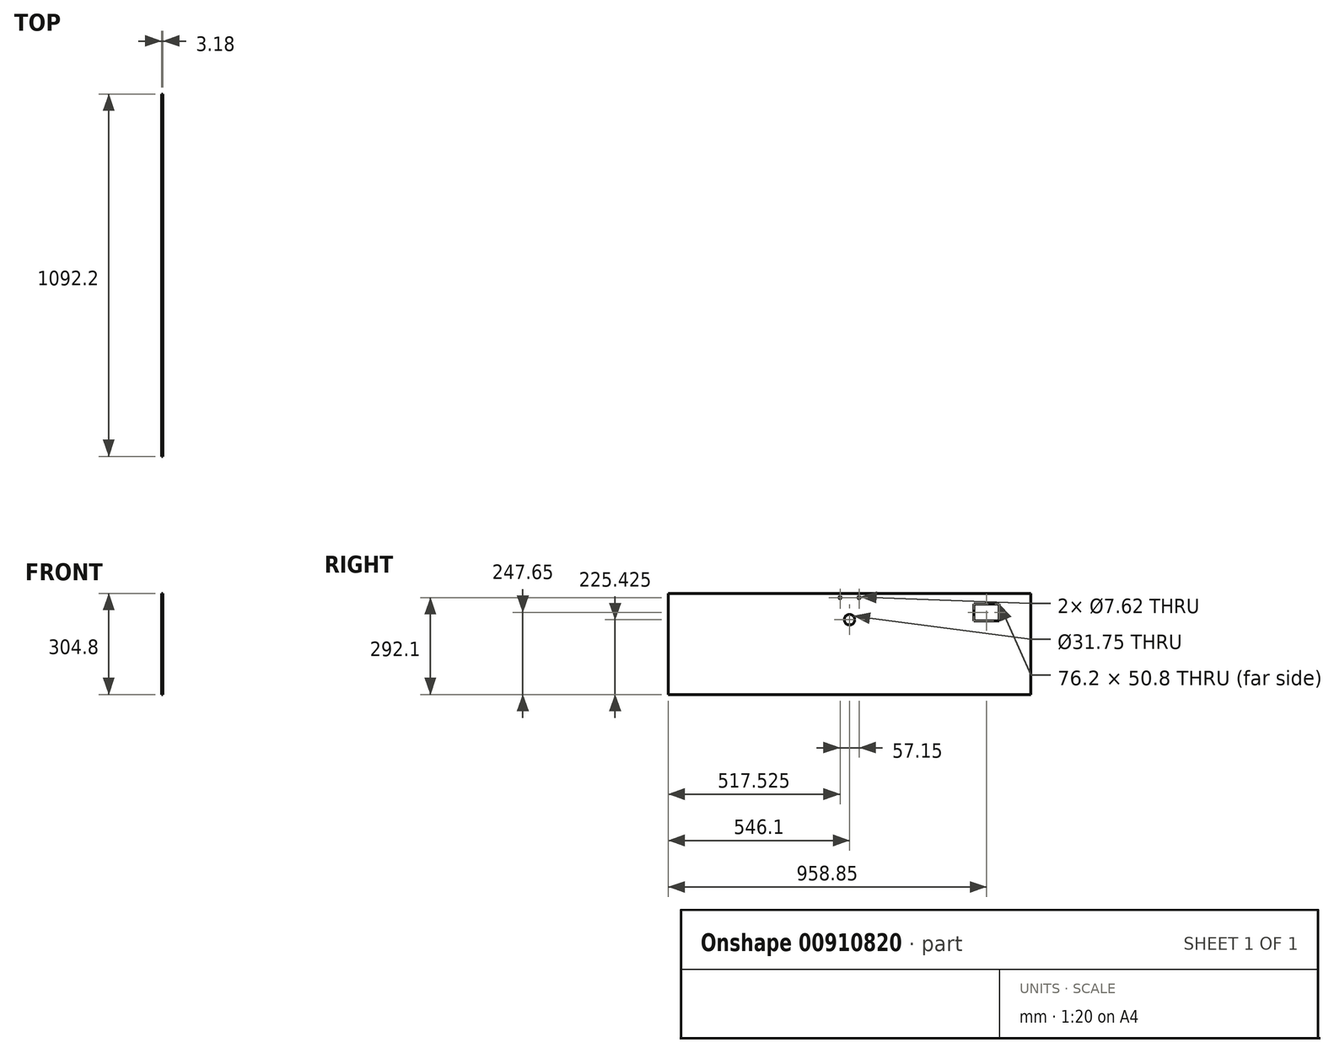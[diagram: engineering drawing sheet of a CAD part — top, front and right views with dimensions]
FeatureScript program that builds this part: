
annotation { "Feature Type Name" : "Feature", "Feature Type Description" : "" }
export const myFeature = defineFeature(function(context is Context, id is Id, definition is map)
    precondition{}
    {
        {
            var Q0;
            Q0=qCreatedBy(makeId("Right.planeOp"),FACE);
            var sketch = newSketch(context, id + "F0", { "sketchPlane" : qUnion([Q0])});
            skLineSegment(sketch, "E0.bottom", {"start": v(0, 0) * mm, "end": v(1092.2, 0) * mm});
            skLineSegment(sketch, "E0.top", {"start": v(0, 304.8) * mm, "end": v(1092.2, 304.8) * mm});
            skLineSegment(sketch, "E0.left", {"start": v(0, 0) * mm, "end": v(0, 304.8) * mm});
            skLineSegment(sketch, "E0.right", {"start": v(1092.2, 0) * mm, "end": v(1092.2, 304.8) * mm});
            skLineSegment(sketch, "E1.bottom", {"start": v(920.75, 222.25) * mm, "end": v(996.95, 222.25) * mm});
            skLineSegment(sketch, "E1.top", {"start": v(920.75, 273.05) * mm, "end": v(996.95, 273.05) * mm});
            skLineSegment(sketch, "E1.left", {"start": v(920.75, 222.25) * mm, "end": v(920.75, 273.05) * mm});
            skLineSegment(sketch, "E1.right", {"start": v(996.95, 222.25) * mm, "end": v(996.95, 273.05) * mm});
            skCircle(sketch, "E2", {"center": v(546.1, 225.43) * mm, "radius": 15.88 * mm});
            skPoint(sketch, "E2.centerSnap0", {"position": v(546.1, 304.8) * mm});
            skCircle(sketch, "E3", {"center": v(517.52, 292.1) * mm, "radius": 3.81 * mm});
            skCircle(sketch, "E4", {"center": v(574.68, 292.1) * mm, "radius": 3.81 * mm});
            skSolve(sketch);
        }
        {
            var Q0;
            Q0 = qSketchRegion(id + "F0", true);
            extrude(context, id + "F1", {"entities" : qUnion([Q0]), "depth" : 3.17 * mm, "offsetDistance" : 25.4 * mm});
        }
    });
